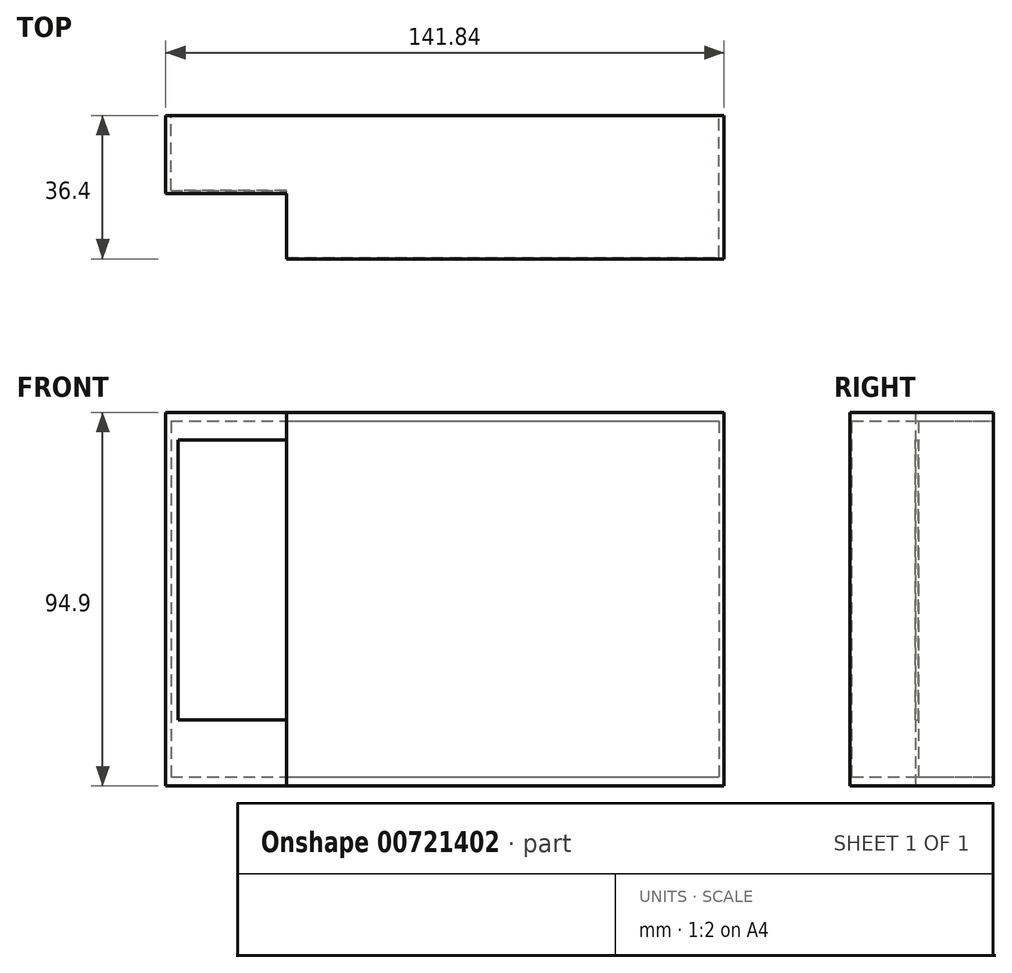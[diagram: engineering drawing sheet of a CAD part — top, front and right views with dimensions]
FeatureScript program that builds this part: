
annotation { "Feature Type Name" : "Feature", "Feature Type Description" : "" }
export const myFeature = defineFeature(function(context is Context, id is Id, definition is map)
    precondition{}
    {
        {
            var Q0;
            Q0=qCreatedBy(makeId("Front.planeOp"),FACE);
            var sketch = newSketch(context, id + "F0", { "sketchPlane" : qUnion([Q0])});
            skLineSegment(sketch, "E0.bottom", {"start": v(70.92, -47.45) * mm, "end": v(-70.92, -47.45) * mm});
            skLineSegment(sketch, "E0.top", {"start": v(70.92, 47.45) * mm, "end": v(-70.92, 47.45) * mm});
            skLineSegment(sketch, "E0.left", {"start": v(70.92, -47.45) * mm, "end": v(70.92, 47.45) * mm});
            skLineSegment(sketch, "E0.right", {"start": v(-70.92, -47.45) * mm, "end": v(-70.92, 47.45) * mm});
            skPoint(sketch, "E0.middle", {"position": v(0, 0) * mm});
            skPoint(sketch, "E1.middle", {"position": v(-70.92, 0) * mm});
            skLineSegment(sketch, "E2", {"start": v(-40.27, 47.45) * mm, "end": v(-40.27, -47.45) * mm});
            skLineSegment(sketch, "E3", {"start": v(-67.78, 47.45) * mm, "end": v(-67.78, -47.45) * mm});
            skLineSegment(sketch, "E4.bottom", {"start": v(-67.78, 40.45) * mm, "end": v(-40.27, 40.45) * mm});
            skLineSegment(sketch, "E4.top", {"start": v(-67.78, -30.7) * mm, "end": v(-40.27, -30.7) * mm});
            skLineSegment(sketch, "E4.left", {"start": v(-67.78, 40.45) * mm, "end": v(-67.78, -30.7) * mm});
            skLineSegment(sketch, "E4.right", {"start": v(-40.27, 40.45) * mm, "end": v(-40.27, -30.7) * mm});
            skSolve(sketch);
        }
        {
            var Q0;
            Q0 = qSketchRegion(id + "F0", true);
            extrude(context, id + "F1", {"entities" : qUnion([Q0]), "depth" : 36.4 * mm, "offsetDistance" : 25 * mm});
        }
        {
            var Q0;
            Q0=makeQuery(id+"F1.opExtrude","SWEPT_FACE",FACE,{"disambiguationData":[OSD([sQuery(id+"F0.wireOp",EDGE,"E0.bottom")])]});
            var sketch = newSketch(context, id + "F2", { "sketchPlane" : qUnion([Q0])});
            skLineSegment(sketch, "E5", {"start": v(-65.57, 36.4) * mm, "end": v(-40.27, 36.4) * mm});
            skLineSegment(sketch, "E6", {"start": v(-40.27, 36.4) * mm, "end": v(-40.27, 19.75) * mm});
            skLineSegment(sketch, "E7", {"start": v(-70.92, 19.75) * mm, "end": v(-40.27, 19.75) * mm});
            skSolve(sketch);
        }
        {
            var Q0;
            Q0 = qSketchRegion(id + "F2", true);
            var Q1;
            {var subQ5=sQuery(id+"F2.wireOp",EDGE,"E5");Q1=makeQuery(id+"F2.imprint","IMPRINT",FACE,{"disambiguationData":[TD([[makeQuery(id+"F2.imprint","IMPRINT",EDGE,{"derivedFrom":subQ5}),1.0]])]});}
            extrude(context, id + "F3", {"entities" : qUnion([Q0, Q1]), "operationType" : NewBodyOperationType.REMOVE, "oppositeDirection" : true, "depth" : 94.9 * mm, "offsetDistance" : 25 * mm});
        }
        {
            var Q0;
            Q0=makeQuery(id+"F1.opExtrude","CAP_FACE",FACE,{"disambiguationData":[OSD([sQuery(id+"F0.wireOp",EDGE,"E0.bottom"),sQuery(id+"F0.wireOp",EDGE,"E0.top"),sQuery(id+"F0.wireOp",EDGE,"E0.left"),sQuery(id+"F0.wireOp",EDGE,"E0.right"),sQuery(id+"F0.wireOp",EDGE,"E4.bottom"),sQuery(id+"F0.wireOp",EDGE,"E4.top"),sQuery(id+"F0.wireOp",EDGE,"E4.left"),sQuery(id+"F0.wireOp",EDGE,"E4.right")])],"isStart":true});
            var sketch = newSketch(context, id + "F4", { "sketchPlane" : qUnion([Q0])});
            skLineSegment(sketch, "E8.bottom", {"start": v(69.59, 45.2) * mm, "end": v(-69.59, 45.2) * mm});
            skLineSegment(sketch, "E8.top", {"start": v(69.59, -45.2) * mm, "end": v(-69.59, -45.2) * mm});
            skLineSegment(sketch, "E8.left", {"start": v(69.59, 45.2) * mm, "end": v(69.59, -45.2) * mm});
            skLineSegment(sketch, "E8.right", {"start": v(-69.59, 45.2) * mm, "end": v(-69.59, -45.2) * mm});
            skPoint(sketch, "E8.middle", {"position": v(0, 0) * mm});
            skSolve(sketch);
        }
        {
            var Q0;
            Q0=makeQuery(id+"F4.imprint","IMPRINT",FACE,{"disambiguationData":[TD([[makeQuery(id+"F4.imprint","IMPRINT",EDGE,{"derivedFrom":makeQuery(id+"F1.opExtrude","CAP_EDGE",EDGE,{"disambiguationData":[OSD([sQuery(id+"F0.wireOp",EDGE,"E4.bottom")])],"isStart":true})}),1.0]])]});
            var Q1;
            Q1=makeQuery(id+"F4.imprint","IMPRINT",FACE,{"disambiguationData":[TD([[makeQuery(id+"F4.imprint","IMPRINT",EDGE,{"derivedFrom":sQuery(id+"F4.wireOp",EDGE,"E8.bottom")}),1.0]])]});
            extrude(context, id + "F5", {"entities" : qUnion([Q0, Q1]), "operationType" : NewBodyOperationType.REMOVE, "oppositeDirection" : true, "depth" : 19 * mm, "offsetDistance" : 25 * mm});
        }
        {
            var Q0;
            Q0=makeQuery(id+"F5.boolean.opBoolean","COPY",FACE,{"derivedFrom":makeQuery(id+"F5.opExtrude","CAP_FACE",FACE,{"disambiguationData":[OSD([sQuery(id+"F4.wireOp",EDGE,"E8.bottom"),sQuery(id+"F4.wireOp",EDGE,"E8.top"),sQuery(id+"F4.wireOp",EDGE,"E8.left"),sQuery(id+"F4.wireOp",EDGE,"E8.right")])],"isStart":false})});
            var sketch = newSketch(context, id + "F6", { "sketchPlane" : qUnion([Q0])});
            skLineSegment(sketch, "E9.bottom", {"start": v(-69.59, 45.2) * mm, "end": v(40.23, 45.2) * mm});
            skLineSegment(sketch, "E9.top", {"start": v(-69.59, -45.2) * mm, "end": v(40.23, -45.2) * mm});
            skLineSegment(sketch, "E9.left", {"start": v(-69.59, 45.2) * mm, "end": v(-69.59, -45.2) * mm});
            skLineSegment(sketch, "E9.right", {"start": v(40.23, 45.2) * mm, "end": v(40.23, -45.2) * mm});
            skSolve(sketch);
        }
        {
            var Q0;
            Q0=makeQuery(id+"F6.imprint","IMPRINT",FACE,{"disambiguationData":[TD([[makeQuery(id+"F6.imprint","IMPRINT",EDGE,{"derivedFrom":sQuery(id+"F6.wireOp",EDGE,"E9.bottom")}),1.0]])]});
            extrude(context, id + "F7", {"entities" : qUnion([Q0]), "operationType" : NewBodyOperationType.REMOVE, "oppositeDirection" : true, "depth" : 17 * mm, "offsetDistance" : 25 * mm});
        }
    });
